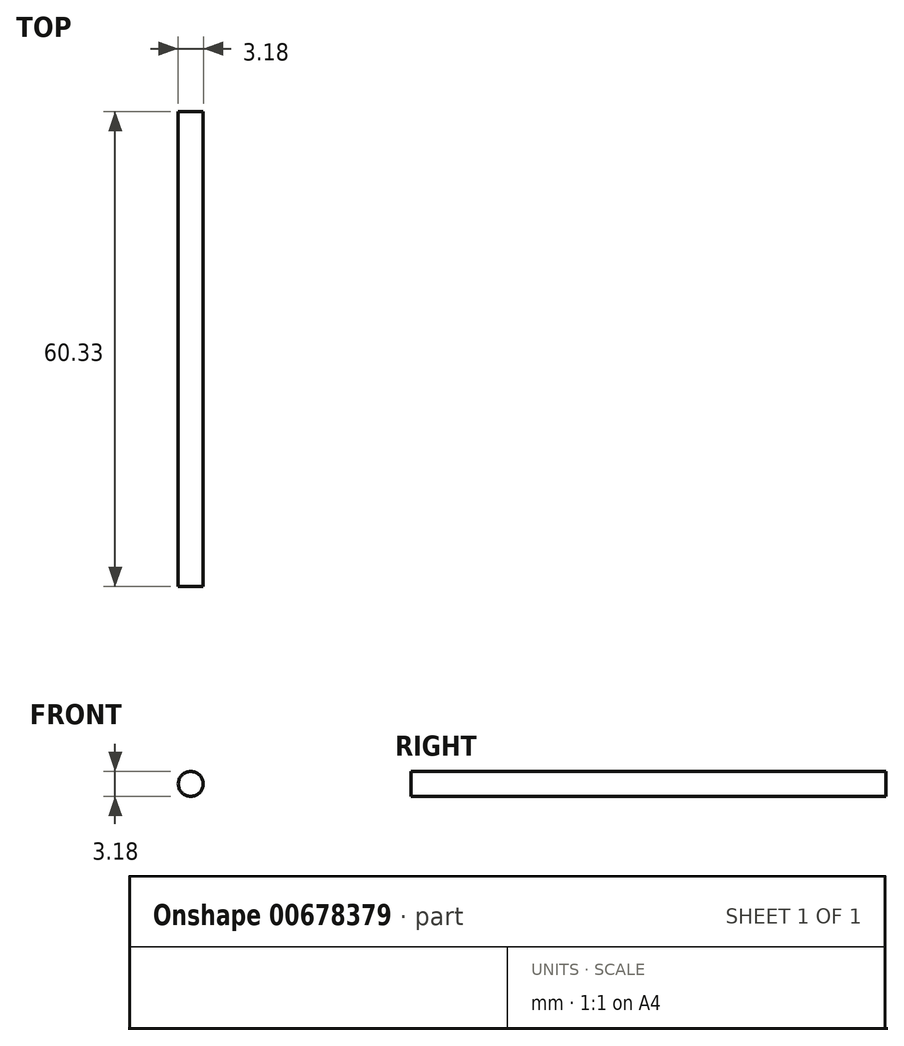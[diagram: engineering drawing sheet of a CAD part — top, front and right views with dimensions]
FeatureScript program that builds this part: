
annotation { "Feature Type Name" : "Feature", "Feature Type Description" : "" }
export const myFeature = defineFeature(function(context is Context, id is Id, definition is map)
    precondition{}
    {
        {
            var Q0;
            Q0=qCreatedBy(makeId("Front.planeOp"),FACE);
            var sketch = newSketch(context, id + "F0", { "sketchPlane" : qUnion([Q0])});
            skCircle(sketch, "E0", {"center": v(0, 0) * mm, "radius": 1.59 * mm});
            skSolve(sketch);
        }
        {
            var Q0;
            Q0=makeQuery(id+"F0.imprint","IMPRINT",FACE,{"disambiguationData":[TD([[makeQuery(id+"F0.imprint","IMPRINT",EDGE,{"derivedFrom":sQuery(id+"F0.wireOp",EDGE,"E0")}),1.0]])]});
            extrude(context, id + "F1", {"entities" : qUnion([Q0]), "depth" : 60.32 * mm, "offsetDistance" : 25.4 * mm});
        }
    });
